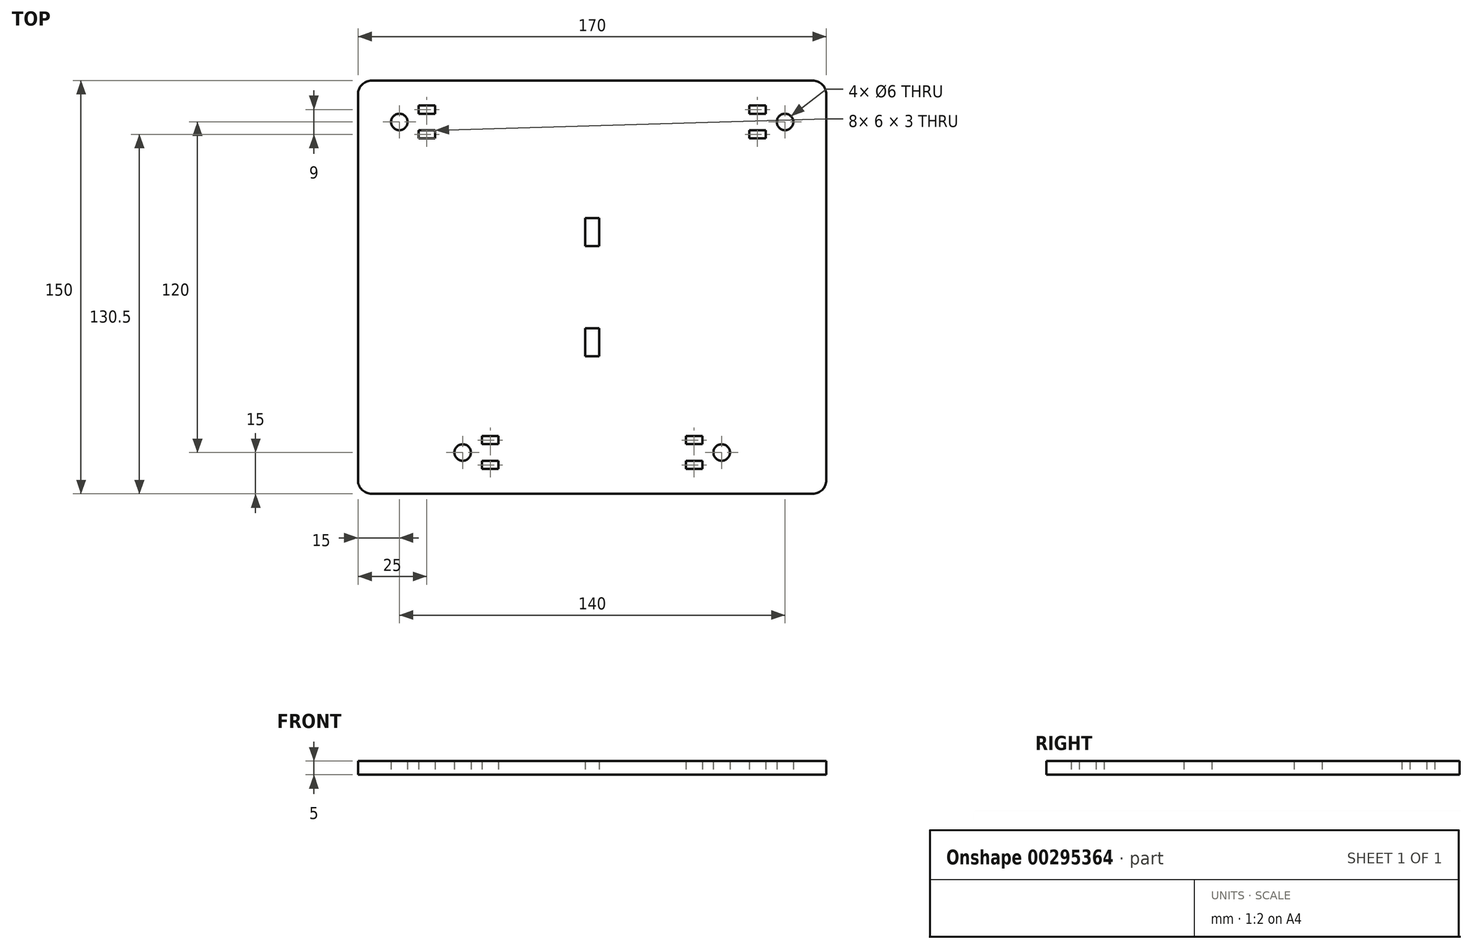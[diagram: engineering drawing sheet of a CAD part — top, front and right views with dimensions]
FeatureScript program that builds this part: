
annotation { "Feature Type Name" : "Feature", "Feature Type Description" : "" }
export const myFeature = defineFeature(function(context is Context, id is Id, definition is map)
    precondition{}
    {
        {
            var Q0;
            Q0=qCreatedBy(makeId("Top.planeOp"),FACE);
            var sketch = newSketch(context, id + "F0", { "sketchPlane" : qUnion([Q0])});
            skCircle(sketch, "E0", {"center": v(-70, 60) * mm, "radius": 3 * mm});
            skCircle(sketch, "E1.MirrorC", {"center": v(70, 60) * mm, "radius": 3 * mm});
            skCircle(sketch, "E2", {"center": v(-47, -60) * mm, "radius": 3 * mm});
            skCircle(sketch, "E3.MirrorC", {"center": v(47, -60) * mm, "radius": 3 * mm});
            skPoint(sketch, "E4", {"position": v(0, 0) * mm});
            skLineSegment(sketch, "E5.top", {"start": v(80, 75) * mm, "end": v(-80, 75) * mm});
            skLineSegment(sketch, "E5.left", {"start": v(85, -70) * mm, "end": v(85, 70) * mm});
            skLineSegment(sketch, "E5.right", {"start": v(-85, -70) * mm, "end": v(-85, 70) * mm});
            skLineSegment(sketch, "E6", {"start": v(-80, -75) * mm, "end": v(80, -75) * mm});
            skPoint(sketch, "E7.positionSnap0", {"position": v(85, 0) * mm});
            skPoint(sketch, "E7.positionSnap1", {"position": v(0, 75) * mm});
            skLineSegment(sketch, "E8.bottom", {"start": v(-63, 66) * mm, "end": v(-57, 66) * mm});
            skLineSegment(sketch, "E8.top", {"start": v(-63, 63) * mm, "end": v(-57, 63) * mm});
            skLineSegment(sketch, "E8.left", {"start": v(-63, 66) * mm, "end": v(-63, 63) * mm});
            skLineSegment(sketch, "E8.right", {"start": v(-57, 66) * mm, "end": v(-57, 63) * mm});
            skLineSegment(sketch, "E9.bottom", {"start": v(-63, 57) * mm, "end": v(-57, 57) * mm});
            skLineSegment(sketch, "E9.top", {"start": v(-63, 54) * mm, "end": v(-57, 54) * mm});
            skLineSegment(sketch, "E9.left", {"start": v(-63, 57) * mm, "end": v(-63, 54) * mm});
            skLineSegment(sketch, "E9.right", {"start": v(-57, 57) * mm, "end": v(-57, 54) * mm});
            skLineSegment(sketch, "E10.bottom", {"start": v(-40, -54) * mm, "end": v(-34, -54) * mm});
            skLineSegment(sketch, "E10.top", {"start": v(-40, -57) * mm, "end": v(-34, -57) * mm});
            skLineSegment(sketch, "E10.left", {"start": v(-40, -54) * mm, "end": v(-40, -57) * mm});
            skLineSegment(sketch, "E10.right", {"start": v(-34, -54) * mm, "end": v(-34, -57) * mm});
            skLineSegment(sketch, "E11.bottom", {"start": v(-40, -63) * mm, "end": v(-34, -63) * mm});
            skLineSegment(sketch, "E11.top", {"start": v(-40, -66) * mm, "end": v(-34, -66) * mm});
            skLineSegment(sketch, "E11.left", {"start": v(-40, -63) * mm, "end": v(-40, -66) * mm});
            skLineSegment(sketch, "E11.right", {"start": v(-34, -63) * mm, "end": v(-34, -66) * mm});
            skLineSegment(sketch, "E12.bottom", {"start": v(57, 66) * mm, "end": v(63, 66) * mm});
            skLineSegment(sketch, "E12.top", {"start": v(57, 63) * mm, "end": v(63, 63) * mm});
            skLineSegment(sketch, "E12.left", {"start": v(57, 66) * mm, "end": v(57, 63) * mm});
            skLineSegment(sketch, "E12.right", {"start": v(63, 66) * mm, "end": v(63, 63) * mm});
            skLineSegment(sketch, "E13.bottom", {"start": v(57, 57) * mm, "end": v(63, 57) * mm});
            skLineSegment(sketch, "E13.top", {"start": v(57, 54) * mm, "end": v(63, 54) * mm});
            skLineSegment(sketch, "E13.left", {"start": v(57, 57) * mm, "end": v(57, 54) * mm});
            skLineSegment(sketch, "E13.right", {"start": v(63, 57) * mm, "end": v(63, 54) * mm});
            skLineSegment(sketch, "E14.bottom", {"start": v(34, -54) * mm, "end": v(40, -54) * mm});
            skLineSegment(sketch, "E14.top", {"start": v(34, -57) * mm, "end": v(40, -57) * mm});
            skLineSegment(sketch, "E14.left", {"start": v(34, -54) * mm, "end": v(34, -57) * mm});
            skLineSegment(sketch, "E14.right", {"start": v(40, -54) * mm, "end": v(40, -57) * mm});
            skLineSegment(sketch, "E15.bottom", {"start": v(34, -63) * mm, "end": v(40, -63) * mm});
            skLineSegment(sketch, "E15.top", {"start": v(34, -66) * mm, "end": v(40, -66) * mm});
            skLineSegment(sketch, "E15.left", {"start": v(34, -63) * mm, "end": v(34, -66) * mm});
            skLineSegment(sketch, "E15.right", {"start": v(40, -63) * mm, "end": v(40, -66) * mm});
            skLineSegment(sketch, "E16.bottom", {"start": v(2.55, 14.95) * mm, "end": v(-2.55, 14.95) * mm});
            skLineSegment(sketch, "E16.top", {"start": v(2.55, 25.05) * mm, "end": v(-2.55, 25.05) * mm});
            skLineSegment(sketch, "E16.left", {"start": v(2.55, 14.95) * mm, "end": v(2.55, 25.05) * mm});
            skLineSegment(sketch, "E16.right", {"start": v(-2.55, 14.95) * mm, "end": v(-2.55, 25.05) * mm});
            skPoint(sketch, "E16.middle", {"position": v(0, 20) * mm});
            skLineSegment(sketch, "E17.bottom", {"start": v(2.55, -25.05) * mm, "end": v(-2.55, -25.05) * mm});
            skLineSegment(sketch, "E17.top", {"start": v(2.55, -14.95) * mm, "end": v(-2.55, -14.95) * mm});
            skLineSegment(sketch, "E17.left", {"start": v(2.55, -25.05) * mm, "end": v(2.55, -14.95) * mm});
            skLineSegment(sketch, "E17.right", {"start": v(-2.55, -25.05) * mm, "end": v(-2.55, -14.95) * mm});
            skPoint(sketch, "E17.middle", {"position": v(0, -20) * mm});
            skPoint(sketch, "E18.visualSharp", {"position": v(-85, 75) * mm});
            skArc(sketch, "E18.filletArc", {"start": v(-80, 75) * mm, "mid": v(-83.54, 73.54) * mm, "end": v(-85, 70) * mm});
            skPoint(sketch, "E19.visualSharp", {"position": v(85, 75) * mm});
            skArc(sketch, "E19.filletArc", {"start": v(85, 70) * mm, "mid": v(83.54, 73.54) * mm, "end": v(80, 75) * mm});
            skPoint(sketch, "E20.visualSharp", {"position": v(85, -75) * mm});
            skArc(sketch, "E20.filletArc", {"start": v(80, -75) * mm, "mid": v(83.54, -73.54) * mm, "end": v(85, -70) * mm});
            skPoint(sketch, "E21.visualSharp", {"position": v(-85, -75) * mm});
            skArc(sketch, "E21.filletArc", {"start": v(-85, -70) * mm, "mid": v(-83.54, -73.54) * mm, "end": v(-80, -75) * mm});
            skSolve(sketch);
        }
        {
            var Q0;
            Q0=makeQuery(id+"F0.imprint","IMPRINT",FACE,{"disambiguationData":[TD([[makeQuery(id+"F0.imprint","IMPRINT",EDGE,{"derivedFrom":sQuery(id+"F0.wireOp",EDGE,"E0")}),-1.0]])]});
            extrude(context, id + "F1", {"entities" : qUnion([Q0]), "depth" : 5 * mm});
        }
    });
